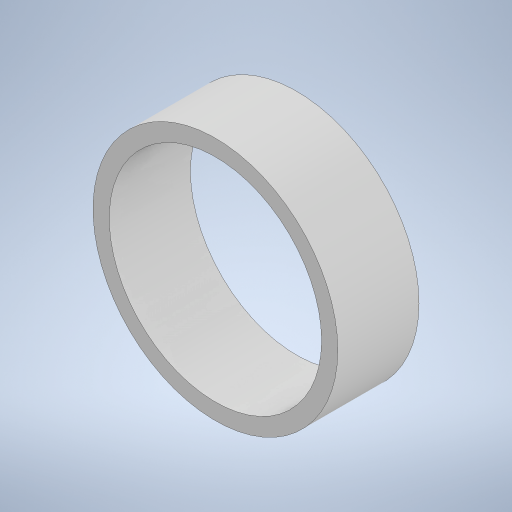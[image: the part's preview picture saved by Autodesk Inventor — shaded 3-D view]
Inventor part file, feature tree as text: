
AUTODESK INVENTOR PART (.ipt)
format: ipt  version: 2024 (Build 280153000, 153)  size: 228,352 bytes
history: native  units: mm
features: extrude x2, sketch x2
ambient origin geometry x8: Origin, YZ Plane, XZ Plane, XY Plane, X Axis, Y Axis, Z Axis, Center Point
bodies: Solid1 (feature_tree)
feature tree (4):
  extrude  "Extrusion1"  Depth=20.0mm TaperAngle=0.0deg
  extrude  "Extrusion2"  TaperAngle=0.0deg  [1 undecoded]
  sketch  "Sketch1"  dims[d0=60.3mm d1=20.0mm d2=0.0mm]
  sketch  "Sketch2"  dims[d3=52.3mm d4=0.0mm d5=0.0mm]
note: 1 required parameter value undecoded (feature->parameter linkage not recoverable at this tier; creation-order binding heuristic only, values carry confidence <= 0.55)
